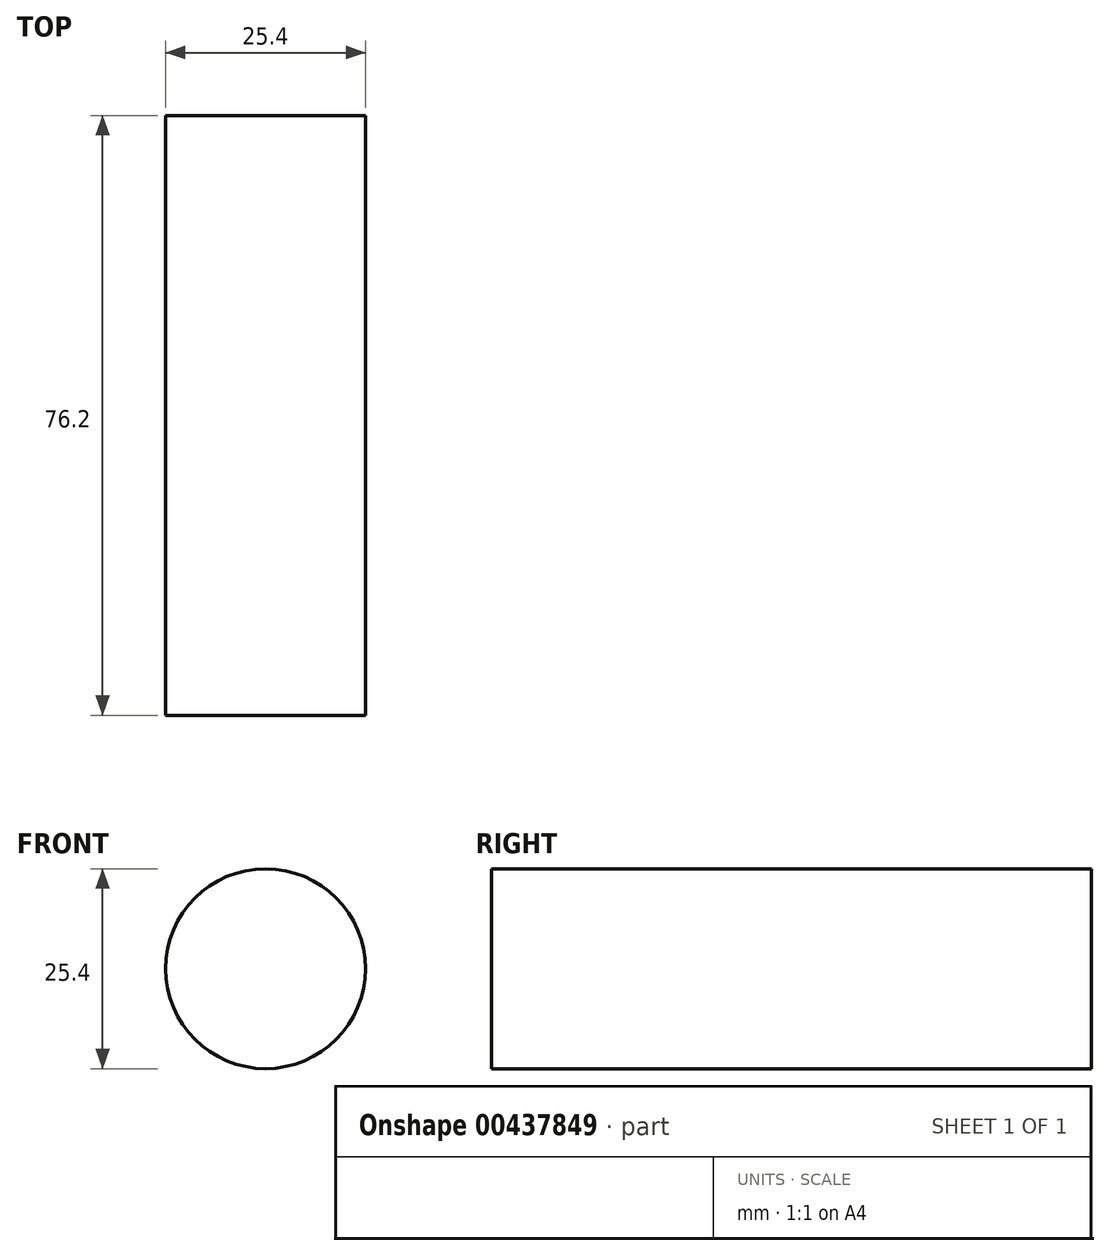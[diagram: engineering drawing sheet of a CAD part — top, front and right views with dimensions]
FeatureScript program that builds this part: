
annotation { "Feature Type Name" : "Feature", "Feature Type Description" : "" }
export const myFeature = defineFeature(function(context is Context, id is Id, definition is map)
    precondition{}
    {
        {
            var Q0;
            Q0=qCreatedBy(makeId("Front.planeOp"),FACE);
            var sketch = newSketch(context, id + "F0", { "sketchPlane" : qUnion([Q0])});
            skCircle(sketch, "E0", {"center": v(-12.22, 12.41) * mm, "radius": 12.7 * mm});
            skSolve(sketch);
        }
        {
            var Q0;
            Q0 = qSketchRegion(id + "F0", true);
            extrude(context, id + "F1", {"entities" : qUnion([Q0]), "depth" : 76.2 * mm});
        }
    });
